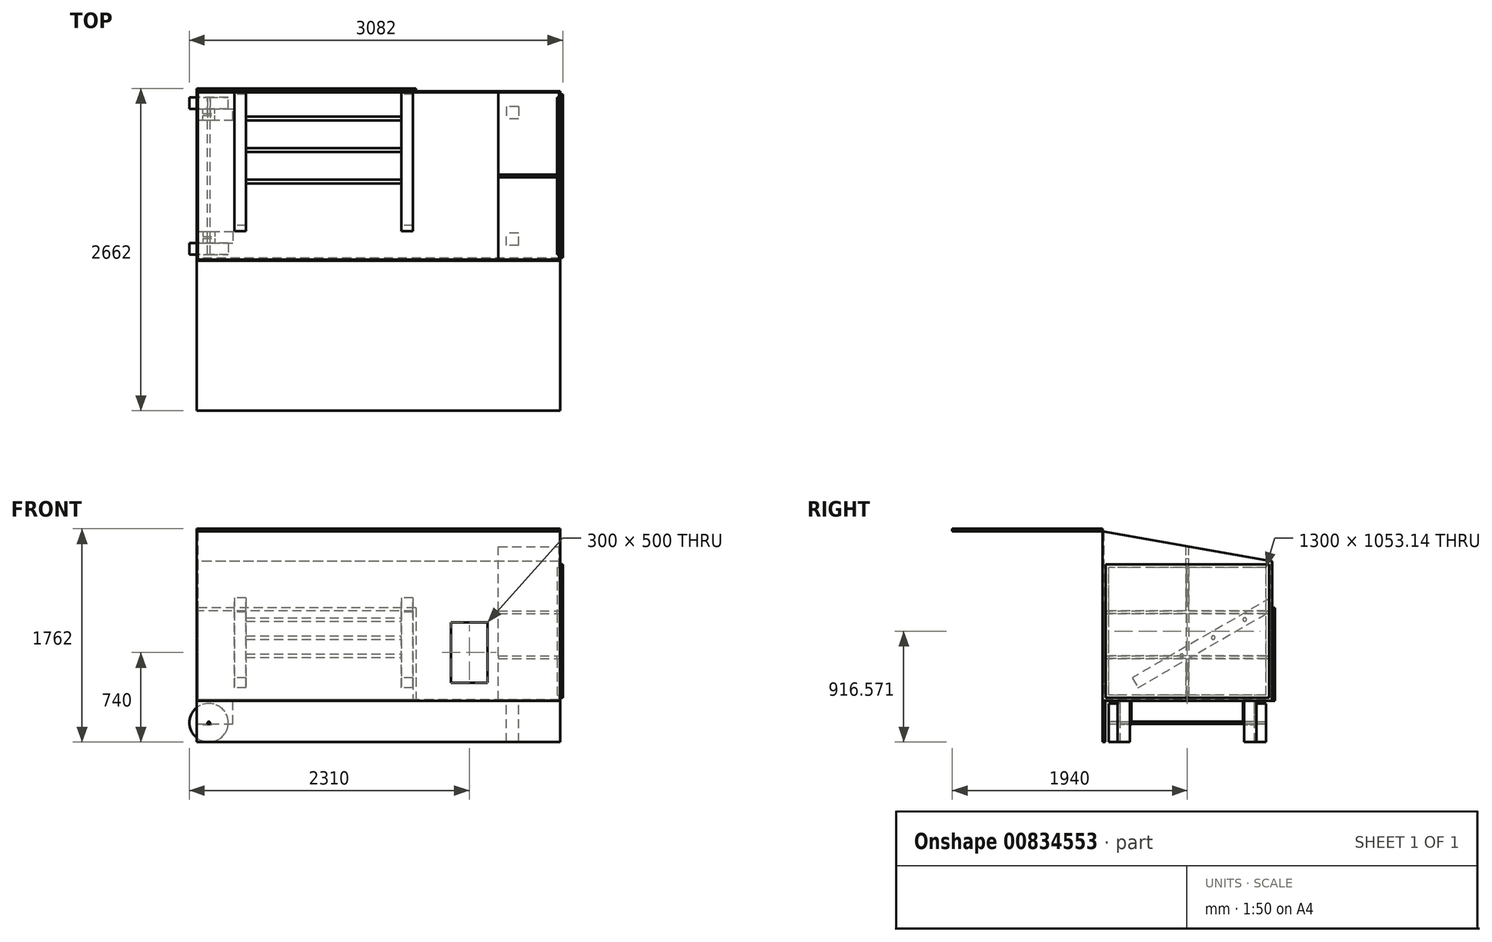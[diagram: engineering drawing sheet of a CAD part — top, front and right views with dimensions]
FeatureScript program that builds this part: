
annotation { "Feature Type Name" : "Feature", "Feature Type Description" : "" }
export const myFeature = defineFeature(function(context is Context, id is Id, definition is map)
    precondition{}
    {
        {
            assignVariable(context, id + "F0", {"variableType" : VariableType.LENGTH, "name" : "WheelDia", "lengthValue" : 320 * mm});
        }
        {
            assignVariable(context, id + "F1", {"variableType" : VariableType.LENGTH, "name" : "Clearence", "lengthValue" : 20 * mm});
        }
        {
            assignVariable(context, id + "F2", {"variableType" : VariableType.LENGTH, "name" : "FeetHeight", "lengthValue" : getVariable(context, 'WheelDia') + getVariable(context, 'Clearence')});
        }
        {
            assignVariable(context, id + "F3", {"variableType" : VariableType.LENGTH, "name" : "Height", "lengthValue" : (20 * 70) * mm});
        }
        {
            var Q0;
            Q0=qCreatedBy(makeId("Top.planeOp"),FACE);
            cPlane(context, id + "F4", {"entities" : qUnion([Q0]), "cplaneType" : CPlaneType.OFFSET, "offset" : getVariable(context, 'FeetHeight'), "width" : 150 * mm, "height" : 150 * mm});
        }
        {
            var Q0;
            Q0=qCreatedBy(id+"F4.planeOp",FACE);
            var sketch = newSketch(context, id + "F5", { "sketchPlane" : qUnion([Q0])});
            skLineSegment(sketch, "E0.bottom", {"start": v(1500, -700) * mm, "end": v(-1500, -700) * mm});
            skLineSegment(sketch, "E0.top", {"start": v(1500, 700) * mm, "end": v(-1500, 700) * mm});
            skLineSegment(sketch, "E0.left", {"start": v(1500, -700) * mm, "end": v(1500, 700) * mm});
            skLineSegment(sketch, "E0.right", {"start": v(-1500, -700) * mm, "end": v(-1500, 700) * mm});
            skPoint(sketch, "E0.middle", {"position": v(0, 0) * mm});
            skSolve(sketch);
        }
        {
            var Q0;
            Q0 = qSketchRegion(id + "F5", true);
            extrude(context, id + "F6", {"entities" : qUnion([Q0]), "depth" : getVariable(context, 'Height'), "offsetDistance" : 25 * mm});
        }
        {
            var Q0;
            Q0=makeQuery(id+"F6.opExtrude","CAP_FACE",FACE,{"disambiguationData":[OSD([sQuery(id+"F5.wireOp",EDGE,"E0.bottom"),sQuery(id+"F5.wireOp",EDGE,"E0.top"),sQuery(id+"F5.wireOp",EDGE,"E0.left"),sQuery(id+"F5.wireOp",EDGE,"E0.right")])],"isStart":false});
            shell(context, id + "F7", {"entities" : qUnion([Q0]), "thickness" : 10 * mm});
        }
        {
            assignVariable(context, id + "F8", {"name" : "RedeDepth", "anyValue" : 500});
        }
        {
            var Q0;
            Q0=makeQuery(id+"F6.opExtrude","SWEPT_FACE",FACE,{"disambiguationData":[OSD([sQuery(id+"F5.wireOp",EDGE,"E0.right")])]});
            var sketch = newSketch(context, id + "F9", { "sketchPlane" : qUnion([Q0])});
            skLineSegment(sketch, "E1", {"start": v(851.23, 1766.67) * mm, "end": v(-923.64, 1453.7) * mm});
            skLineSegment(sketch, "E2", {"start": v(-923.64, 1453.7) * mm, "end": v(-1018.41, 1991.17) * mm});
            skLineSegment(sketch, "E3", {"start": v(-1018.41, 1991.17) * mm, "end": v(692.6, 2227) * mm});
            skLineSegment(sketch, "E4", {"start": v(692.6, 2227) * mm, "end": v(851.23, 1766.67) * mm});
            skSolve(sketch);
        }
        {
            var Q0;
            Q0 = qSketchRegion(id + "F9", true);
            extrude(context, id + "F10", {"entities" : qUnion([Q0]), "operationType" : NewBodyOperationType.REMOVE, "endBound" : BoundingType.THROUGH_ALL, "oppositeDirection" : true, "depth" : 25 * mm, "offsetDistance" : 25 * mm});
        }
        {
            var Q0;
            Q0=makeQuery(id+"F7.opShell","OFFSET_FACE",FACE,{"disambiguationData":[OSD([sQuery(id+"F5.wireOp",EDGE,"E0.left")])]});
            var sketch = newSketch(context, id + "F11", { "sketchPlane" : qUnion([Q0])});
            skLineSegment(sketch, "E5.bottom", {"start": v(11, 350) * mm, "end": v(-11, 350) * mm});
            skLineSegment(sketch, "E5.top", {"start": v(11, 1614.63) * mm, "end": v(-11, 1614.63) * mm});
            skLineSegment(sketch, "E5.left", {"start": v(11, 350) * mm, "end": v(11, 1614.63) * mm});
            skLineSegment(sketch, "E5.right", {"start": v(-11, 350) * mm, "end": v(-11, 1614.63) * mm});
            skPoint(sketch, "E5.middle", {"position": v(0, 982.32) * mm});
            skLineSegment(sketch, "E6.bottom", {"start": v(690, 690) * mm, "end": v(-690, 690) * mm});
            skLineSegment(sketch, "E6.top", {"start": v(690, 712) * mm, "end": v(-690, 712) * mm});
            skLineSegment(sketch, "E6.left", {"start": v(690, 690) * mm, "end": v(690, 712) * mm});
            skLineSegment(sketch, "E6.right", {"start": v(-690, 690) * mm, "end": v(-690, 712) * mm});
            skPoint(sketch, "E6.middle", {"position": v(0, 701) * mm});
            skLineSegment(sketch, "E7.bottom", {"start": v(690, 1062) * mm, "end": v(-690, 1062) * mm});
            skLineSegment(sketch, "E7.top", {"start": v(690, 1084) * mm, "end": v(-690, 1084) * mm});
            skLineSegment(sketch, "E7.left", {"start": v(690, 1062) * mm, "end": v(690, 1084) * mm});
            skLineSegment(sketch, "E7.right", {"start": v(-690, 1062) * mm, "end": v(-690, 1084) * mm});
            skPoint(sketch, "E7.middle", {"position": v(0, 1073) * mm});
            skSolve(sketch);
        }
        {
            var Q0;
            Q0 = qSketchRegion(id + "F11", true);
            extrude(context, id + "F12", {"entities" : qUnion([Q0]), "depth" : (getVariable(context, 'RedeDepth')) * mm, "offsetDistance" : 25 * mm});
        }
        {
            var Q0;
            Q0=makeQuery(id+"F6.opExtrude","SWEPT_FACE",FACE,{"disambiguationData":[OSD([sQuery(id+"F5.wireOp",EDGE,"E0.left")])]});
            var sketch = newSketch(context, id + "F13", { "sketchPlane" : qUnion([Q0])});
            skLineSegment(sketch, "E8.bottom", {"start": v(650, 390) * mm, "end": v(-650, 390) * mm});
            skLineSegment(sketch, "E8.top", {"start": v(650, 1443.14) * mm, "end": v(-650, 1443.14) * mm});
            skLineSegment(sketch, "E8.left", {"start": v(650, 390) * mm, "end": v(650, 1443.14) * mm});
            skLineSegment(sketch, "E8.right", {"start": v(-650, 390) * mm, "end": v(-650, 1443.14) * mm});
            skPoint(sketch, "E8.middle", {"position": v(0, 916.57) * mm});
            skSolve(sketch);
        }
        {
            var Q0;
            Q0 = qSketchRegion(id + "F13", true);
            extrude(context, id + "F14", {"entities" : qUnion([Q0]), "operationType" : NewBodyOperationType.REMOVE, "oppositeDirection" : true, "depth" : 25 * mm, "offsetDistance" : 25 * mm});
        }
        {
            var Q0;
            Q0=makeQuery(id+"F6.opExtrude","SWEPT_FACE",FACE,{"disambiguationData":[OSD([sQuery(id+"F5.wireOp",EDGE,"E0.left")])]});
            var sketch = newSketch(context, id + "F15", { "sketchPlane" : qUnion([Q0])});
            skLineSegment(sketch, "E9.bottom", {"start": v(675, 365) * mm, "end": v(-675, 365) * mm});
            skLineSegment(sketch, "E9.top", {"start": v(675, 1468.14) * mm, "end": v(-675, 1468.14) * mm});
            skLineSegment(sketch, "E9.left", {"start": v(675, 365) * mm, "end": v(675, 1468.14) * mm});
            skLineSegment(sketch, "E9.right", {"start": v(-675, 365) * mm, "end": v(-675, 1468.14) * mm});
            skPoint(sketch, "E9.middle", {"position": v(0, 916.57) * mm});
            skSolve(sketch);
        }
        {
            var Q0;
            Q0 = qSketchRegion(id + "F15", true);
            extrude(context, id + "F16", {"entities" : qUnion([Q0]), "depth" : 22 * mm, "offsetDistance" : 25 * mm});
        }
        {
            var Q0;
            Q0=qCreatedBy(makeId("Right.planeOp"),FACE);
            cPlane(context, id + "F17", {"entities" : qUnion([Q0]), "cplaneType" : CPlaneType.OFFSET, "offset" : 190 * mm, "width" : 150 * mm, "height" : 150 * mm});
        }
        {
            var Q0;
            Q0=qCreatedBy(id+"F17.planeOp",FACE);
            var sketch = newSketch(context, id + "F18", { "sketchPlane" : qUnion([Q0])});
            skLineSegment(sketch, "E10", {"start": v(690, 1193.14) * mm, "end": v(-454.66, 532.27) * mm});
            skLineSegment(sketch, "E11", {"start": v(-454.66, 532.27) * mm, "end": v(-407.16, 450) * mm});
            skLineSegment(sketch, "E12", {"start": v(-407.16, 450) * mm, "end": v(690, 1083.45) * mm});
            skLineSegment(sketch, "E13", {"start": v(690, 1083.45) * mm, "end": v(690, 1193.14) * mm});
            skSolve(sketch);
        }
        {
            var Q0;
            Q0 = qSketchRegion(id + "F18", true);
            extrude(context, id + "F19", {"entities" : qUnion([Q0]), "depth" : 95 * mm, "offsetDistance" : 25 * mm});
        }
        {
            var Q0;
            Q0=makeQuery(id+"F19.opExtrude","SWEPT_BODY",BODY,{"disambiguationData":[OSD([sQuery(id+"F18.wireOp",EDGE,"E10"),sQuery(id+"F18.wireOp",EDGE,"E11"),sQuery(id+"F18.wireOp",EDGE,"E12"),sQuery(id+"F18.wireOp",EDGE,"E13")])]});
            var Q1;
            Q1=makeQuery(id+"F10.boolean.opBoolean","INTERSECT",EDGE,{"derivedFrom":[makeQuery(id+"F6.opExtrude","SWEPT_FACE",FACE,{"disambiguationData":[OSD([sQuery(id+"F5.wireOp",EDGE,"E0.top")])]}),makeQuery(id+"F10.opExtrude","SWEPT_FACE",FACE,{"disambiguationData":[OSD([sQuery(id+"F9.wireOp",EDGE,"E1")])]})]});
            transform(context, id + "F20", {"entities" : qUnion([Q0]), "transformType" : TransformType.TRANSLATION_DISTANCE, "transformDirection" : qUnion([Q1]), "distance" : 1377 * mm, "makeCopy" : true});
        }
        {
            var Q0;
            Q0=makeQuery(id+"F19.opExtrude","CAP_FACE",FACE,{"disambiguationData":[OSD([sQuery(id+"F18.wireOp",EDGE,"E10"),sQuery(id+"F18.wireOp",EDGE,"E11"),sQuery(id+"F18.wireOp",EDGE,"E12"),sQuery(id+"F18.wireOp",EDGE,"E13")])],"isStart":true});
            var sketch = newSketch(context, id + "F21", { "sketchPlane" : qUnion([Q0])});
            skCircle(sketch, "E14", {"center": v(-473.5, 1013.3) * mm, "radius": 15 * mm});
            skCircle(sketch, "E15", {"center": v(-213.69, 863.3) * mm, "radius": 15 * mm});
            skLineSegment(sketch, "E16", {"start": v(-473.5, 1013.3) * mm, "end": v(46.12, 713.3) * mm, "construction": true});
            skCircle(sketch, "E17", {"center": v(46.12, 713.3) * mm, "radius": 15 * mm});
            skSolve(sketch);
        }
        {
            var Q0;
            Q0 = qSketchRegion(id + "F21", true);
            extrude(context, id + "F22", {"entities" : qUnion([Q0]), "endBound" : BoundingType.UP_TO_NEXT, "depth" : 25 * mm, "offsetDistance" : 25 * mm});
        }
        {
            var Q0;
            Q0=makeQuery(id+"F6.opExtrude","SWEPT_FACE",FACE,{"disambiguationData":[OSD([sQuery(id+"F5.wireOp",EDGE,"E0.bottom")])]});
            var sketch = newSketch(context, id + "F23", { "sketchPlane" : qUnion([Q0])});
            skLineSegment(sketch, "E18.bottom", {"start": v(600, 990) * mm, "end": v(900, 990) * mm});
            skLineSegment(sketch, "E18.top", {"start": v(600, 490) * mm, "end": v(900, 490) * mm});
            skLineSegment(sketch, "E18.left", {"start": v(600, 990) * mm, "end": v(600, 490) * mm});
            skLineSegment(sketch, "E18.right", {"start": v(900, 990) * mm, "end": v(900, 490) * mm});
            skSolve(sketch);
        }
        {
            var Q0;
            Q0 = qSketchRegion(id + "F23", true);
            extrude(context, id + "F24", {"entities" : qUnion([Q0]), "operationType" : NewBodyOperationType.REMOVE, "oppositeDirection" : true, "depth" : 25 * mm, "offsetDistance" : 25 * mm});
        }
        {
            var Q0;
            Q0=makeQuery(id+"F6.opExtrude","SWEPT_FACE",FACE,{"disambiguationData":[OSD([sQuery(id+"F5.wireOp",EDGE,"E0.right")])]});
            var sketch = newSketch(context, id + "F25", { "sketchPlane" : qUnion([Q0])});
            skLineSegment(sketch, "E19.bottom", {"start": v(700, 1740) * mm, "end": v(1940, 1740) * mm});
            skLineSegment(sketch, "E19.top", {"start": v(700, 1762) * mm, "end": v(1940, 1762) * mm});
            skLineSegment(sketch, "E19.left", {"start": v(700, 1740) * mm, "end": v(700, 1762) * mm});
            skLineSegment(sketch, "E19.right", {"start": v(1940, 1740) * mm, "end": v(1940, 1762) * mm});
            skSolve(sketch);
        }
        {
            var Q0;
            Q0 = qSketchRegion(id + "F25", true);
            var Q1;
            Q1=makeQuery(id+"F6.opExtrude","SWEPT_FACE",FACE,{"disambiguationData":[OSD([sQuery(id+"F5.wireOp",EDGE,"E0.left")])]});
            extrude(context, id + "F26", {"entities" : qUnion([Q0]), "endBound" : BoundingType.UP_TO_SURFACE, "oppositeDirection" : true, "depth" : 25 * mm, "endBoundEntityFace" : qUnion([Q1]), "offsetDistance" : 25 * mm});
        }
        {
            var Q0;
            Q0=makeQuery(id+"F6.opExtrude","SWEPT_FACE",FACE,{"disambiguationData":[OSD([sQuery(id+"F5.wireOp",EDGE,"E0.top")])]});
            var sketch = newSketch(context, id + "F27", { "sketchPlane" : qUnion([Q0])});
            skLineSegment(sketch, "E20.bottom", {"start": v(-285, 1083.45) * mm, "end": v(1490, 1083.45) * mm});
            skLineSegment(sketch, "E20.top", {"start": v(-285, 350) * mm, "end": v(1490, 350) * mm});
            skLineSegment(sketch, "E20.left", {"start": v(-285, 1083.45) * mm, "end": v(-285, 350) * mm});
            skLineSegment(sketch, "E20.right", {"start": v(1490, 1083.45) * mm, "end": v(1490, 350) * mm});
            skSolve(sketch);
        }
        {
            var Q0;
            Q0 = qSketchRegion(id + "F27", true);
            extrude(context, id + "F28", {"entities" : qUnion([Q0]), "operationType" : NewBodyOperationType.REMOVE, "oppositeDirection" : true, "depth" : 25 * mm, "offsetDistance" : 25 * mm});
        }
        {
            var Q0;
            Q0=makeQuery(id+"F6.opExtrude","SWEPT_FACE",FACE,{"disambiguationData":[OSD([sQuery(id+"F5.wireOp",EDGE,"E0.top")])]});
            var sketch = newSketch(context, id + "F29", { "sketchPlane" : qUnion([Q0])});
            skLineSegment(sketch, "E21.bottom", {"start": v(-310, 1108.45) * mm, "end": v(1500, 1108.45) * mm});
            skLineSegment(sketch, "E21.top", {"start": v(-310, 340) * mm, "end": v(1500, 340) * mm});
            skLineSegment(sketch, "E21.left", {"start": v(-310, 1108.45) * mm, "end": v(-310, 340) * mm});
            skLineSegment(sketch, "E21.right", {"start": v(1500, 1108.45) * mm, "end": v(1500, 340) * mm});
            skSolve(sketch);
        }
        {
            var Q0;
            Q0 = qSketchRegion(id + "F29", true);
            extrude(context, id + "F30", {"entities" : qUnion([Q0]), "depth" : 22 * mm, "offsetDistance" : 25 * mm});
        }
        {
            var Q0;
            Q0=makeQuery(id+"F6.opExtrude","CAP_FACE",FACE,{"disambiguationData":[OSD([sQuery(id+"F5.wireOp",EDGE,"E0.bottom"),sQuery(id+"F5.wireOp",EDGE,"E0.top"),sQuery(id+"F5.wireOp",EDGE,"E0.left"),sQuery(id+"F5.wireOp",EDGE,"E0.right")])],"isStart":true});
            var sketch = newSketch(context, id + "F31", { "sketchPlane" : qUnion([Q0])});
            skLineSegment(sketch, "E22.bottom", {"start": v(1500, 700) * mm, "end": v(-1500, 700) * mm});
            skLineSegment(sketch, "E22.top", {"start": v(1500, 678) * mm, "end": v(-1500, 678) * mm});
            skLineSegment(sketch, "E22.left", {"start": v(1500, 700) * mm, "end": v(1500, 678) * mm});
            skLineSegment(sketch, "E22.right", {"start": v(-1500, 700) * mm, "end": v(-1500, 678) * mm});
            skSolve(sketch);
        }
        {
            var Q0;
            Q0 = qSketchRegion(id + "F31", true);
            extrude(context, id + "F32", {"entities" : qUnion([Q0]), "depth" : getVariable(context, 'FeetHeight'), "offsetDistance" : 25 * mm});
        }
        {
            var Q0;
            Q0=makeQuery(id+"F6.opExtrude","CAP_FACE",FACE,{"disambiguationData":[OSD([sQuery(id+"F5.wireOp",EDGE,"E0.bottom"),sQuery(id+"F5.wireOp",EDGE,"E0.top"),sQuery(id+"F5.wireOp",EDGE,"E0.left"),sQuery(id+"F5.wireOp",EDGE,"E0.right")])],"isStart":true});
            var sketch = newSketch(context, id + "F33", { "sketchPlane" : qUnion([Q0])});
            skLineSegment(sketch, "E23.bottom", {"start": v(1156.44, 574.5) * mm, "end": v(1055.23, 574.5) * mm});
            skLineSegment(sketch, "E23.top", {"start": v(1156.44, 473.28) * mm, "end": v(1055.23, 473.28) * mm});
            skLineSegment(sketch, "E23.left", {"start": v(1156.44, 574.5) * mm, "end": v(1156.44, 473.28) * mm});
            skLineSegment(sketch, "E23.right", {"start": v(1055.23, 574.5) * mm, "end": v(1055.23, 473.28) * mm});
            skLineSegment(sketch, "E24.bottom", {"start": v(1156.44, -571.03) * mm, "end": v(1055.23, -571.03) * mm});
            skLineSegment(sketch, "E24.top", {"start": v(1156.44, -469.82) * mm, "end": v(1055.23, -469.82) * mm});
            skLineSegment(sketch, "E24.left", {"start": v(1156.44, -571.03) * mm, "end": v(1156.44, -469.82) * mm});
            skLineSegment(sketch, "E24.right", {"start": v(1055.23, -571.03) * mm, "end": v(1055.23, -469.82) * mm});
            skSolve(sketch);
        }
        {
            var Q0;
            Q0 = qSketchRegion(id + "F33", true);
            extrude(context, id + "F34", {"entities" : qUnion([Q0]), "depth" : getVariable(context, 'FeetHeight'), "offsetDistance" : 25 * mm});
        }
        {
            var Q0;
            Q0=makeQuery(id+"F6.opExtrude","SWEPT_FACE",FACE,{"disambiguationData":[OSD([sQuery(id+"F5.wireOp",EDGE,"E0.bottom")])]});
            cPlane(context, id + "F35", {"entities" : qUnion([Q0]), "cplaneType" : CPlaneType.OFFSET, "offset" : 50 * mm, "oppositeDirection" : true, "width" : 150 * mm, "height" : 150 * mm});
        }
        {
            var Q0;
            Q0=qCreatedBy(id+"F35.planeOp",FACE);
            var sketch = newSketch(context, id + "F36", { "sketchPlane" : qUnion([Q0])});
            skCircle(sketch, "E25", {"center": v(-1400, 160) * mm, "radius": 160 * mm});
            skCircle(sketch, "E26", {"center": v(-1400, 160) * mm, "radius": 10 * mm});
            skSolve(sketch);
        }
        {
            var Q0;
            Q0 = qSketchRegion(id + "F36", true);
            extrude(context, id + "F37", {"entities" : qUnion([Q0]), "oppositeDirection" : true, "depth" : 95 * mm, "offsetDistance" : 25 * mm});
        }
        {
            var Q0;
            Q0=makeQuery(id+"F6.opExtrude","CAP_FACE",FACE,{"disambiguationData":[OSD([sQuery(id+"F5.wireOp",EDGE,"E0.bottom"),sQuery(id+"F5.wireOp",EDGE,"E0.top"),sQuery(id+"F5.wireOp",EDGE,"E0.left"),sQuery(id+"F5.wireOp",EDGE,"E0.right")])],"isStart":true});
            var sketch = newSketch(context, id + "F38", { "sketchPlane" : qUnion([Q0])});
            skLineSegment(sketch, "E27.bottom", {"start": v(-1500, 460) * mm, "end": v(-1200, 460) * mm});
            skLineSegment(sketch, "E27.top", {"start": v(-1500, 555) * mm, "end": v(-1200, 555) * mm});
            skLineSegment(sketch, "E27.left", {"start": v(-1500, 460) * mm, "end": v(-1500, 555) * mm});
            skLineSegment(sketch, "E27.right", {"start": v(-1200, 460) * mm, "end": v(-1200, 555) * mm});
            skSolve(sketch);
        }
        {
            var Q0;
            Q0 = qSketchRegion(id + "F38", true);
            extrude(context, id + "F39", {"entities" : qUnion([Q0]), "depth" : (2 * 95) * mm, "offsetDistance" : 25 * mm});
        }
        {
            var Q0;
            Q0=makeQuery(id+"F39.opExtrude","SWEPT_FACE",FACE,{"disambiguationData":[OSD([sQuery(id+"F38.wireOp",EDGE,"E27.bottom")])]});
            var sketch = newSketch(context, id + "F40", { "sketchPlane" : qUnion([Q0])});
            skArc(sketch, "E28.0", {"start": v(1410, 160) * mm, "mid": v(1400, 170) * mm, "end": v(1390, 160) * mm});
            skLineSegment(sketch, "E29", {"start": v(1410, 150) * mm, "end": v(1410, 160) * mm});
            skLineSegment(sketch, "E30", {"start": v(1390, 150) * mm, "end": v(1390, 160) * mm});
            skLineSegment(sketch, "E31", {"start": v(1410, 150) * mm, "end": v(1390, 150) * mm});
            skSolve(sketch);
        }
        {
            var Q0;
            Q0 = qSketchRegion(id + "F40", true);
            extrude(context, id + "F41", {"entities" : qUnion([Q0]), "operationType" : NewBodyOperationType.REMOVE, "endBound" : BoundingType.THROUGH_ALL, "oppositeDirection" : true, "depth" : 25 * mm, "offsetDistance" : 25 * mm});
        }
        {
            var Q0;
            {var subQ0=sQuery(id+"F38.wireOp",EDGE,"E27.bottom");var subQ1=sQuery(id+"F38.wireOp",EDGE,"E27.top");var subQ2=sQuery(id+"F38.wireOp",EDGE,"E27.left");Q0=makeQuery(id+"F41.boolean.opBoolean","SPLIT",FACE,{"disambiguationData":[TD([makeQuery(id+"F39.opExtrude","SWEPT_FACE",FACE,{"disambiguationData":[OSD([subQ2])]})])],"derivedFrom":makeQuery(id+"F39.opExtrude","CAP_FACE",FACE,{"disambiguationData":[OSD([subQ0,subQ1,subQ2,sQuery(id+"F38.wireOp",EDGE,"E27.right")])],"isStart":false})});}
            var sketch = newSketch(context, id + "F42", { "sketchPlane" : qUnion([Q0])});
            skLineSegment(sketch, "E32.bottom", {"start": v(-1450, 460) * mm, "end": v(-1350, 460) * mm});
            skLineSegment(sketch, "E32.top", {"start": v(-1450, 500) * mm, "end": v(-1350, 500) * mm});
            skLineSegment(sketch, "E32.left", {"start": v(-1450, 460) * mm, "end": v(-1450, 500) * mm});
            skLineSegment(sketch, "E32.right", {"start": v(-1350, 460) * mm, "end": v(-1350, 500) * mm});
            skLineSegment(sketch, "E33.bottom", {"start": v(-1450, 515) * mm, "end": v(-1350, 515) * mm});
            skLineSegment(sketch, "E33.top", {"start": v(-1450, 555) * mm, "end": v(-1350, 555) * mm});
            skLineSegment(sketch, "E33.left", {"start": v(-1450, 515) * mm, "end": v(-1450, 555) * mm});
            skLineSegment(sketch, "E33.right", {"start": v(-1350, 515) * mm, "end": v(-1350, 555) * mm});
            skLineSegment(sketch, "E34", {"start": v(-1400, 320.06) * mm, "end": v(-1400, 548.97) * mm, "construction": true});
            skSolve(sketch);
        }
        {
            var Q0;
            Q0 = qSketchRegion(id + "F42", true);
            extrude(context, id + "F43", {"entities" : qUnion([Q0]), "depth" : 5 * mm, "offsetDistance" : 25 * mm});
        }
        {
            var Q0;
            Q0=makeQuery(id+"F37.opExtrude","SWEPT_BODY",BODY,{"disambiguationData":[OSD([sQuery(id+"F36.wireOp",EDGE,"E25"),sQuery(id+"F36.wireOp",EDGE,"E26")])]});
            var Q1;
            Q1=makeQuery(id+"F39.opExtrude","SWEPT_BODY",BODY,{"disambiguationData":[OSD([sQuery(id+"F38.wireOp",EDGE,"E27.bottom"),sQuery(id+"F38.wireOp",EDGE,"E27.top"),sQuery(id+"F38.wireOp",EDGE,"E27.left"),sQuery(id+"F38.wireOp",EDGE,"E27.right")])]});
            var Q2;
            Q2=makeQuery(id+"F43.opExtrude","SWEPT_BODY",BODY,{"disambiguationData":[OSD([sQuery(id+"F42.wireOp",EDGE,"E33.bottom"),sQuery(id+"F42.wireOp",EDGE,"E33.top"),sQuery(id+"F42.wireOp",EDGE,"E33.left"),sQuery(id+"F42.wireOp",EDGE,"E33.right")])]});
            var Q3;
            Q3=makeQuery(id+"F43.opExtrude","SWEPT_BODY",BODY,{"disambiguationData":[OSD([sQuery(id+"F42.wireOp",EDGE,"E32.bottom"),sQuery(id+"F42.wireOp",EDGE,"E32.top"),sQuery(id+"F42.wireOp",EDGE,"E32.left"),sQuery(id+"F42.wireOp",EDGE,"E32.right")])]});
            var Q4;
            Q4=qCreatedBy(makeId("Front.planeOp"),FACE);
            mirror(context, id + "F44", {"entities" : qUnion([Q0, Q1, Q2, Q3]), "mirrorPlane" : qUnion([Q4])});
        }
        {
            var Q0;
            Q0=makeQuery(id+"F44.opPattern","COPY",FACE,{"derivedFrom":makeQuery(id+"F37.opExtrude","CAP_FACE",FACE,{"disambiguationData":[OSD([sQuery(id+"F36.wireOp",EDGE,"E25"),sQuery(id+"F36.wireOp",EDGE,"E26")])],"isStart":true}),"instanceName":"1"});
            var sketch = newSketch(context, id + "F45", { "sketchPlane" : qUnion([Q0])});
            skCircle(sketch, "E35.0", {"center": v(1400, 160) * mm, "radius": 10 * mm});
            skSolve(sketch);
        }
        {
            var Q0;
            Q0 = qSketchRegion(id + "F45", true);
            var Q1;
            Q1=makeQuery(id+"F37.opExtrude","CAP_FACE",FACE,{"disambiguationData":[OSD([sQuery(id+"F36.wireOp",EDGE,"E25"),sQuery(id+"F36.wireOp",EDGE,"E26")])],"isStart":true});
            extrude(context, id + "F46", {"entities" : qUnion([Q0]), "endBound" : BoundingType.UP_TO_SURFACE, "oppositeDirection" : true, "depth" : 25 * mm, "endBoundEntityFace" : qUnion([Q1]), "offsetDistance" : 25 * mm});
        }
    });
